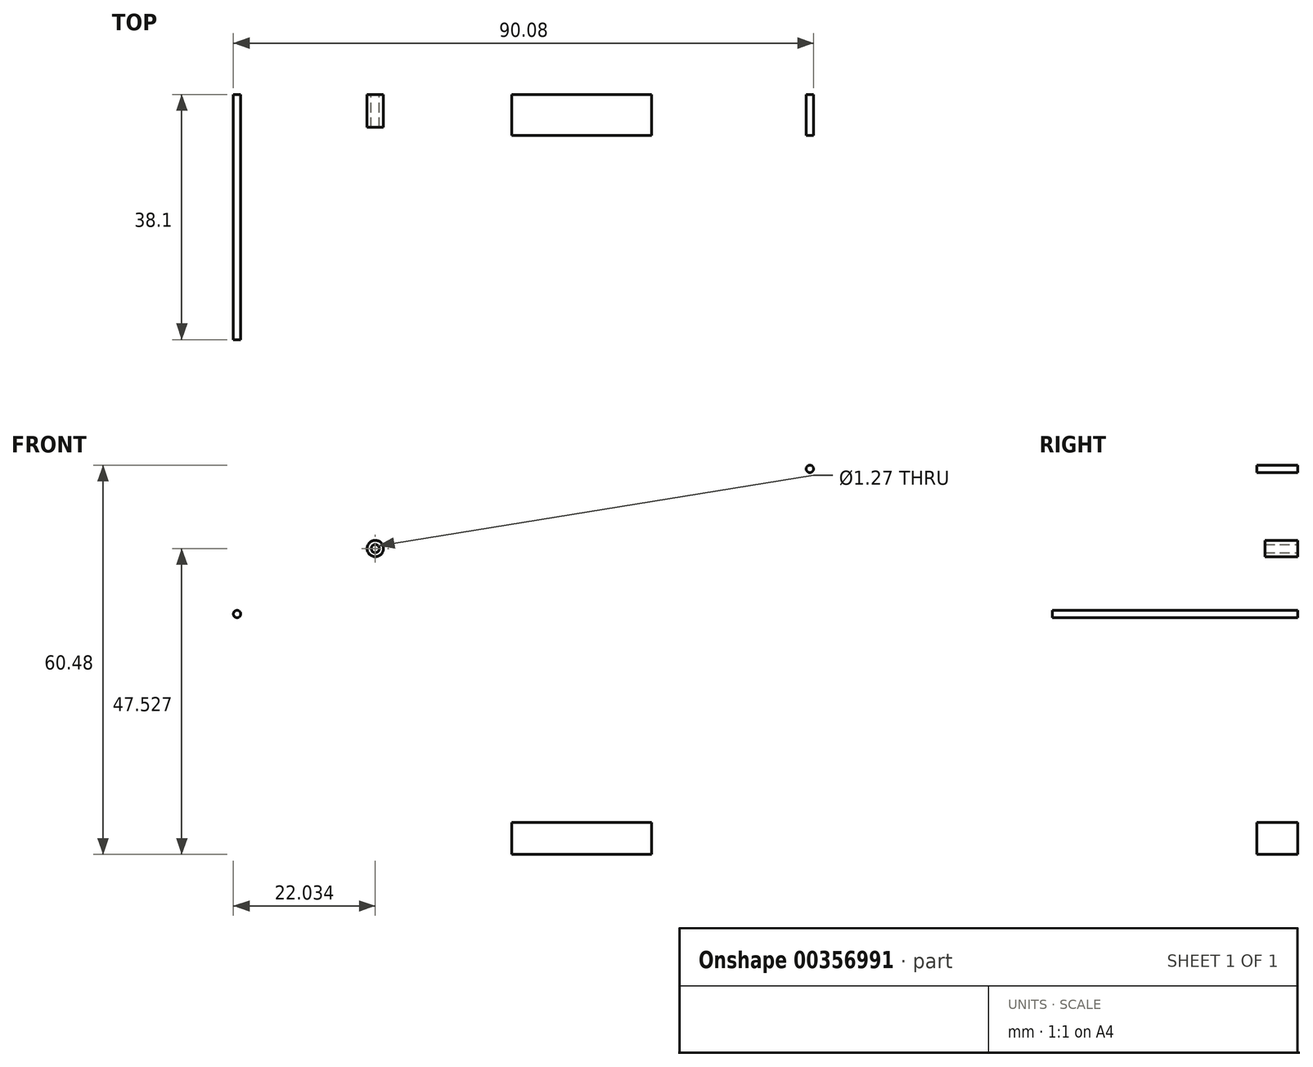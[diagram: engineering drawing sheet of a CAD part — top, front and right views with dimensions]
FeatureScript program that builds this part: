
annotation { "Feature Type Name" : "Feature", "Feature Type Description" : "" }
export const myFeature = defineFeature(function(context is Context, id is Id, definition is map)
    precondition{}
    {
        {
            var Q0;
            Q0=qCreatedBy(makeId("Front.planeOp"),FACE);
            var sketch = newSketch(context, id + "F0", { "sketchPlane" : qUnion([Q0])});
            skCircle(sketch, "E0", {"center": v(-41.17, 24.3) * mm, "radius": 1.27 * mm});
            skSolve(sketch);
        }
        {
            var Q0;
            Q0 = qSketchRegion(id + "F0", true);
            extrude(context, id + "F1", {"entities" : qUnion([Q0]), "depth" : 5.08 * mm});
        }
        {
            var Q0;
            Q0=sQuery(id+"F0.wireOp",VERTEX,"E0.center");
            var Q1;
            Q1=makeQuery(id+"F1.opExtrude","SWEPT_BODY",BODY,{"disambiguationData":[OSD([sQuery(id+"F0.wireOp",EDGE,"E0")])]});
            hole(context, id + "F2", {"style" : HoleStyle.SIMPLE, "endStyle" : HoleEndStyle.THROUGH, "oppositeDirection" : true, "holeDiameter" : 1.27 * mm, "isTappedThrough" : true, "tappedDepth" : 12.7 * mm, "tapClearance" : 3, "locations" : qUnion([Q0]), "scope" : qUnion([Q1])});
        }
        {
            var Q0;
            Q0=qCreatedBy(makeId("Front.planeOp"),FACE);
            var sketch = newSketch(context, id + "F3", { "sketchPlane" : qUnion([Q0])});
            skLineSegment(sketch, "E1.bottom", {"start": v(-20, -18.25) * mm, "end": v(1.75, -18.25) * mm});
            skLineSegment(sketch, "E1.top", {"start": v(-20, -23.23) * mm, "end": v(1.75, -23.23) * mm});
            skLineSegment(sketch, "E1.left", {"start": v(-20, -18.25) * mm, "end": v(-20, -23.23) * mm});
            skLineSegment(sketch, "E1.right", {"start": v(1.75, -18.25) * mm, "end": v(1.75, -23.23) * mm});
            skSolve(sketch);
        }
        {
            var Q0;
            Q0 = qSketchRegion(id + "F3", true);
            extrude(context, id + "F4", {"entities" : qUnion([Q0]), "depth" : 6.35 * mm});
        }
        {
            var Q0;
            Q0=qCreatedBy(makeId("Front.planeOp"),FACE);
            var sketch = newSketch(context, id + "F5", { "sketchPlane" : qUnion([Q0])});
            skCircle(sketch, "E2", {"center": v(-62.63, 14.13) * mm, "radius": 0.57 * mm});
            skSolve(sketch);
        }
        {
            var Q0;
            Q0 = qSketchRegion(id + "F5", true);
            extrude(context, id + "F6", {"entities" : qUnion([Q0]), "depth" : 38.1 * mm});
        }
        {
            var Q0;
            Q0=qCreatedBy(makeId("Front.planeOp"),FACE);
            var sketch = newSketch(context, id + "F7", { "sketchPlane" : qUnion([Q0])});
            skCircle(sketch, "E3", {"center": v(26.3, 36.68) * mm, "radius": 0.57 * mm});
            skSolve(sketch);
        }
        {
            var Q0;
            Q0=makeQuery(id+"F7.imprint","IMPRINT",FACE,{"disambiguationData":[TD([[makeQuery(id+"F7.imprint","IMPRINT",EDGE,{"derivedFrom":sQuery(id+"F7.wireOp",EDGE,"E3")}),1.0]])]});
            extrude(context, id + "F8", {"entities" : qUnion([Q0]), "depth" : 6.35 * mm});
        }
    });
